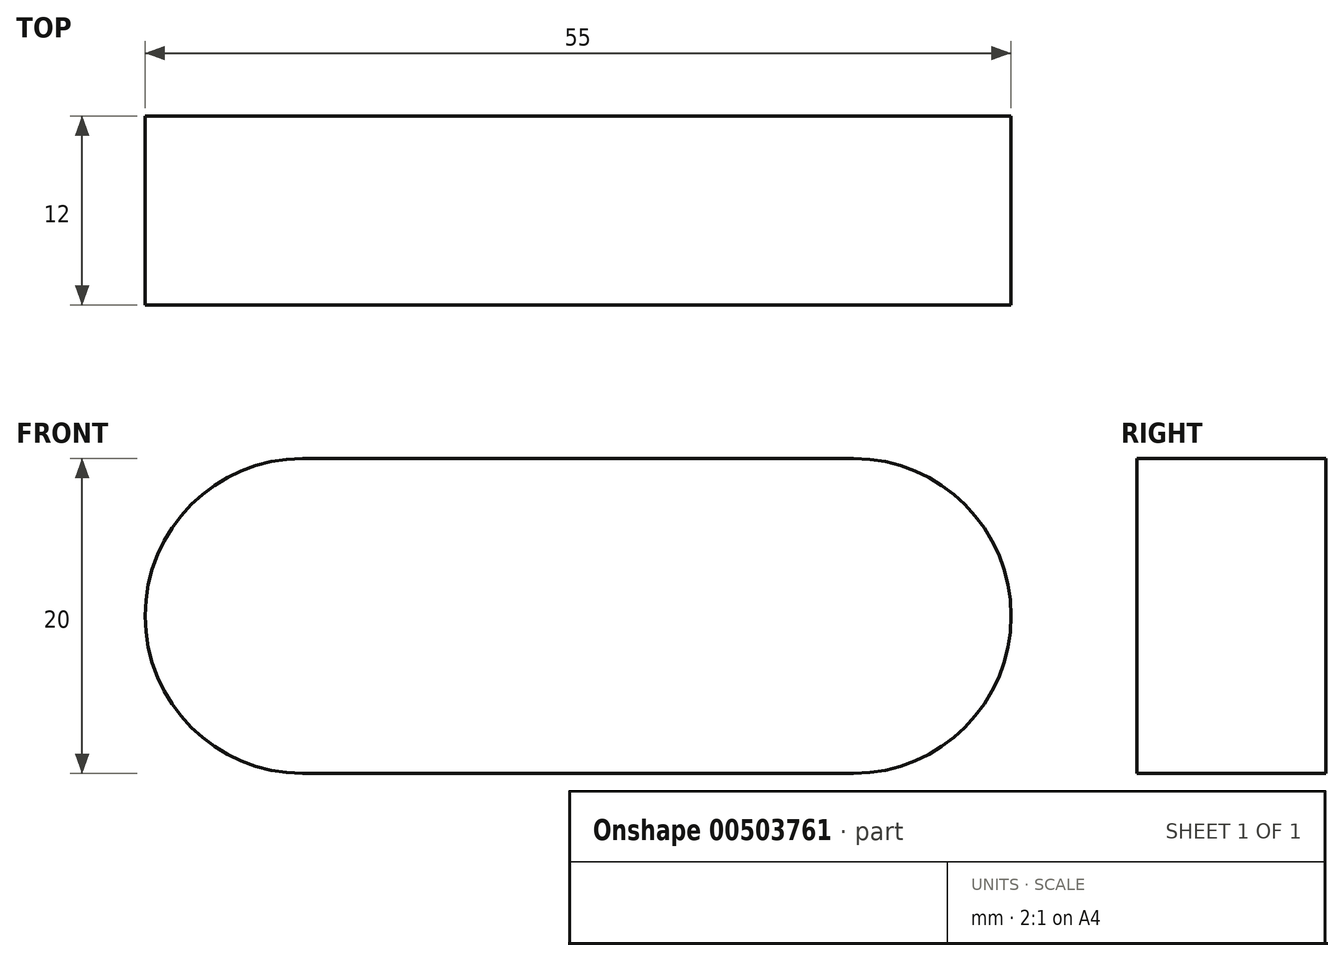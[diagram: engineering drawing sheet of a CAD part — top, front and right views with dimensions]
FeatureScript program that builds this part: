
annotation { "Feature Type Name" : "Feature", "Feature Type Description" : "" }
export const myFeature = defineFeature(function(context is Context, id is Id, definition is map)
    precondition{}
    {
        {
            var Q0;
            Q0=qCreatedBy(makeId("Front.planeOp"),FACE);
            var sketch = newSketch(context, id + "F0", { "sketchPlane" : qUnion([Q0])});
            skArc(sketch, "E0", {"start": v(0, 10) * mm, "mid": v(-10, 0) * mm, "end": v(0, -10) * mm});
            skArc(sketch, "E1", {"start": v(35, -10) * mm, "mid": v(45, 0) * mm, "end": v(35, 10) * mm});
            skLineSegment(sketch, "E2", {"start": v(0, 10) * mm, "end": v(35, 10) * mm});
            skLineSegment(sketch, "E3", {"start": v(35, -10) * mm, "end": v(0, -10) * mm});
            skSolve(sketch);
        }
        {
            var Q0;
            Q0 = qSketchRegion(id + "F0", true);
            extrude(context, id + "F1", {"entities" : qUnion([Q0]), "depth" : 12 * mm});
        }
    });
